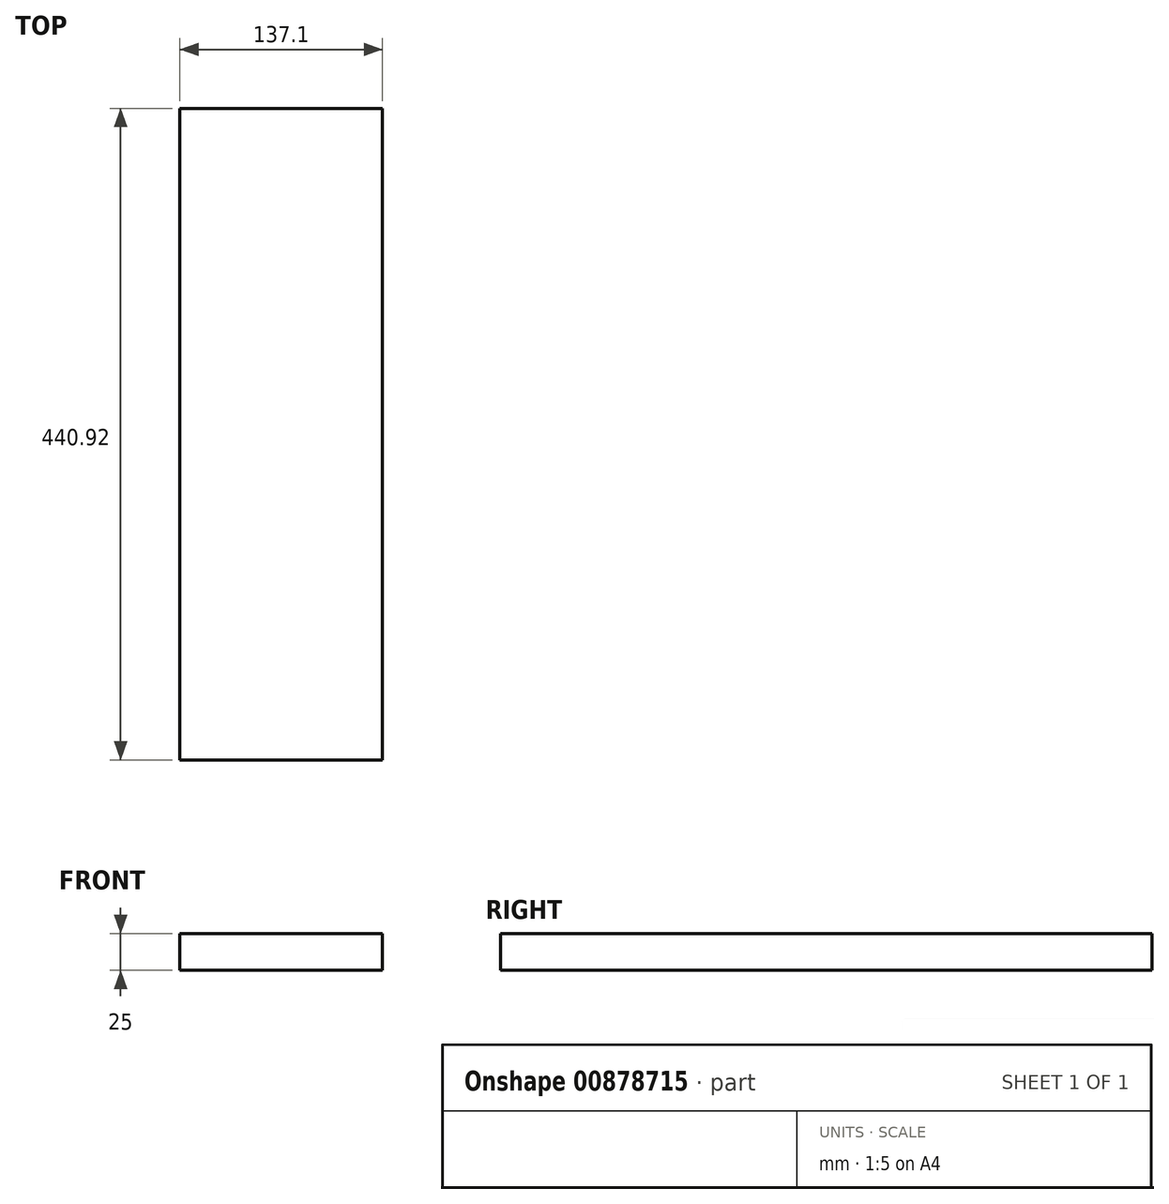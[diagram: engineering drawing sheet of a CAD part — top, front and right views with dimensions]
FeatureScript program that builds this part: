
annotation { "Feature Type Name" : "Feature", "Feature Type Description" : "" }
export const myFeature = defineFeature(function(context is Context, id is Id, definition is map)
    precondition{}
    {
        {
            var Q0;
            Q0=qCreatedBy(makeId("Top.planeOp"),FACE);
            var sketch = newSketch(context, id + "F0", { "sketchPlane" : qUnion([Q0])});
            skLineSegment(sketch, "E0.bottom", {"start": v(-68.55, -220.46) * mm, "end": v(68.55, -220.46) * mm});
            skLineSegment(sketch, "E0.top", {"start": v(-68.55, 220.46) * mm, "end": v(68.55, 220.46) * mm});
            skLineSegment(sketch, "E0.left", {"start": v(-68.55, -220.46) * mm, "end": v(-68.55, 220.46) * mm});
            skLineSegment(sketch, "E0.right", {"start": v(68.55, -220.46) * mm, "end": v(68.55, 220.46) * mm});
            skPoint(sketch, "E0.middle", {"position": v(0, 0) * mm});
            skSolve(sketch);
        }
        {
            var Q0;
            Q0=makeQuery(id+"F0.imprint","IMPRINT",FACE,{"disambiguationData":[TD([[makeQuery(id+"F0.imprint","IMPRINT",EDGE,{"derivedFrom":sQuery(id+"F0.wireOp",EDGE,"E0.bottom")}),1.0]])]});
            extrude(context, id + "F1", {"entities" : qUnion([Q0]), "depth" : 25 * mm, "offsetDistance" : 25 * mm});
        }
    });
